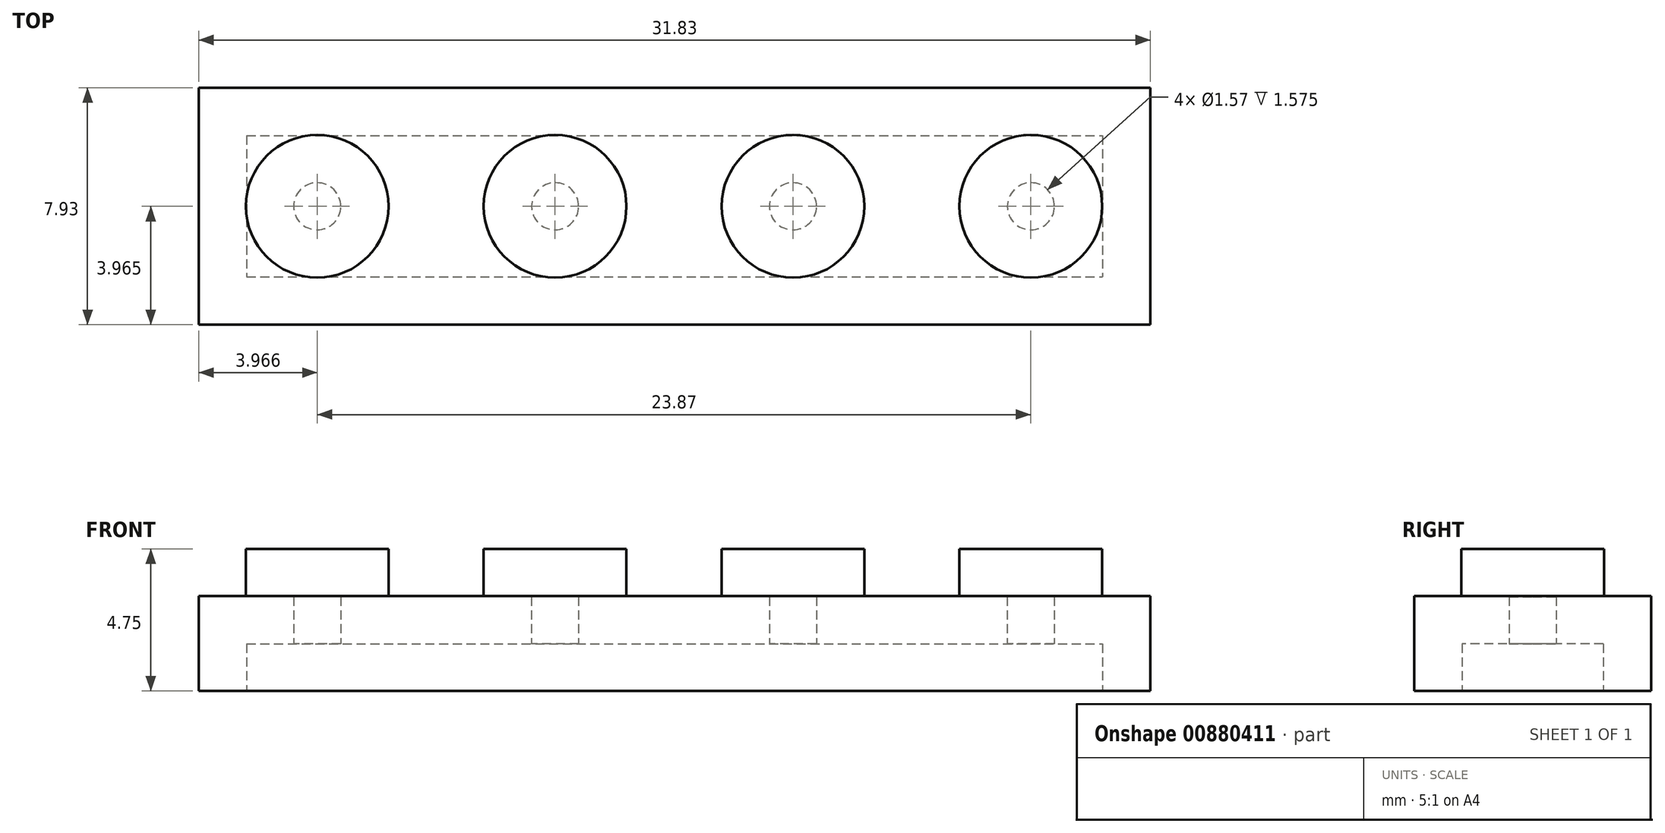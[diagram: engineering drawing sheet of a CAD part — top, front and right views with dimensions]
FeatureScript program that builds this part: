
annotation { "Feature Type Name" : "Feature", "Feature Type Description" : "" }
export const myFeature = defineFeature(function(context is Context, id is Id, definition is map)
    precondition{}
    {
        {
            var Q0;
            Q0=qCreatedBy(makeId("Top.planeOp"),FACE);
            var sketch = newSketch(context, id + "F0", { "sketchPlane" : qUnion([Q0])});
            skLineSegment(sketch, "E0.bottom", {"start": v(-25.72, 19.92) * mm, "end": v(6.1, 19.92) * mm});
            skLineSegment(sketch, "E0.top", {"start": v(-25.72, 12) * mm, "end": v(6.1, 12) * mm});
            skLineSegment(sketch, "E0.left", {"start": v(-25.72, 19.92) * mm, "end": v(-25.72, 12) * mm});
            skLineSegment(sketch, "E0.right", {"start": v(6.1, 19.92) * mm, "end": v(6.1, 12) * mm});
            skLineSegment(sketch, "E1", {"start": v(-25.72, 15.95) * mm, "end": v(6.1, 15.95) * mm, "construction": true});
            skCircle(sketch, "E2", {"center": v(-21.75, 15.95) * mm, "radius": 2.39 * mm});
            skCircle(sketch, "E3", {"center": v(-13.8, 15.95) * mm, "radius": 2.39 * mm});
            skCircle(sketch, "E4", {"center": v(-5.84, 15.95) * mm, "radius": 2.39 * mm});
            skCircle(sketch, "E5", {"center": v(2.12, 15.95) * mm, "radius": 2.39 * mm});
            skSolve(sketch);
        }
        {
            var Q0;
            Q0=makeQuery(id+"F0.imprint","IMPRINT",FACE,{"disambiguationData":[TD([[makeQuery(id+"F0.imprint","IMPRINT",EDGE,{"derivedFrom":sQuery(id+"F0.wireOp",EDGE,"E0.bottom")}),-1.0]])]});
            extrude(context, id + "F1", {"entities" : qUnion([Q0]), "depth" : 3.17 * mm, "offsetDistance" : 25.4 * mm});
        }
        {
            var Q0;
            Q0=makeQuery(id+"F0.imprint","IMPRINT",FACE,{"disambiguationData":[TD([[makeQuery(id+"F0.imprint","IMPRINT",EDGE,{"derivedFrom":sQuery(id+"F0.wireOp",EDGE,"E2")}),1.0]])]});
            var Q1;
            Q1=makeQuery(id+"F0.imprint","IMPRINT",FACE,{"disambiguationData":[TD([[makeQuery(id+"F0.imprint","IMPRINT",EDGE,{"derivedFrom":sQuery(id+"F0.wireOp",EDGE,"E3")}),1.0]])]});
            var Q2;
            Q2=makeQuery(id+"F0.imprint","IMPRINT",FACE,{"disambiguationData":[TD([[makeQuery(id+"F0.imprint","IMPRINT",EDGE,{"derivedFrom":sQuery(id+"F0.wireOp",EDGE,"E4")}),1.0]])]});
            var Q3;
            Q3=makeQuery(id+"F0.imprint","IMPRINT",FACE,{"disambiguationData":[TD([[makeQuery(id+"F0.imprint","IMPRINT",EDGE,{"derivedFrom":sQuery(id+"F0.wireOp",EDGE,"E5")}),1.0]])]});
            extrude(context, id + "F2", {"entities" : qUnion([Q0, Q1, Q2, Q3]), "operationType" : NewBodyOperationType.ADD, "depth" : 4.75 * mm, "offsetDistance" : 25.4 * mm});
        }
        {
            var Q0;
            {var subQ0=sQuery(id+"F0.wireOp",EDGE,"E5");var subQ1=sQuery(id+"F0.wireOp",EDGE,"E4");var subQ2=sQuery(id+"F0.wireOp",EDGE,"E3");var subQ3=sQuery(id+"F0.wireOp",EDGE,"E2");Q0=makeQuery(id+"F2.boolean.opBoolean","MERGE",FACE,{"derivedFrom":[makeQuery(id+"F1.opExtrude","CAP_FACE",FACE,{"disambiguationData":[OSD([sQuery(id+"F0.wireOp",EDGE,"E0.bottom"),sQuery(id+"F0.wireOp",EDGE,"E0.top"),sQuery(id+"F0.wireOp",EDGE,"E0.left"),sQuery(id+"F0.wireOp",EDGE,"E0.right"),subQ3,subQ2,subQ1,subQ0])],"isStart":true}),makeQuery(id+"F2.opExtrude","CAP_FACE",FACE,{"disambiguationData":[OSD([subQ3])],"isStart":true}),makeQuery(id+"F2.opExtrude","CAP_FACE",FACE,{"disambiguationData":[OSD([subQ2])],"isStart":true}),makeQuery(id+"F2.opExtrude","CAP_FACE",FACE,{"disambiguationData":[OSD([subQ1])],"isStart":true}),makeQuery(id+"F2.opExtrude","CAP_FACE",FACE,{"disambiguationData":[OSD([subQ0])],"isStart":true})]});}
            shell(context, id + "F3", {"entities" : qUnion([Q0]), "thickness" : 1.6 * mm});
        }
    });
